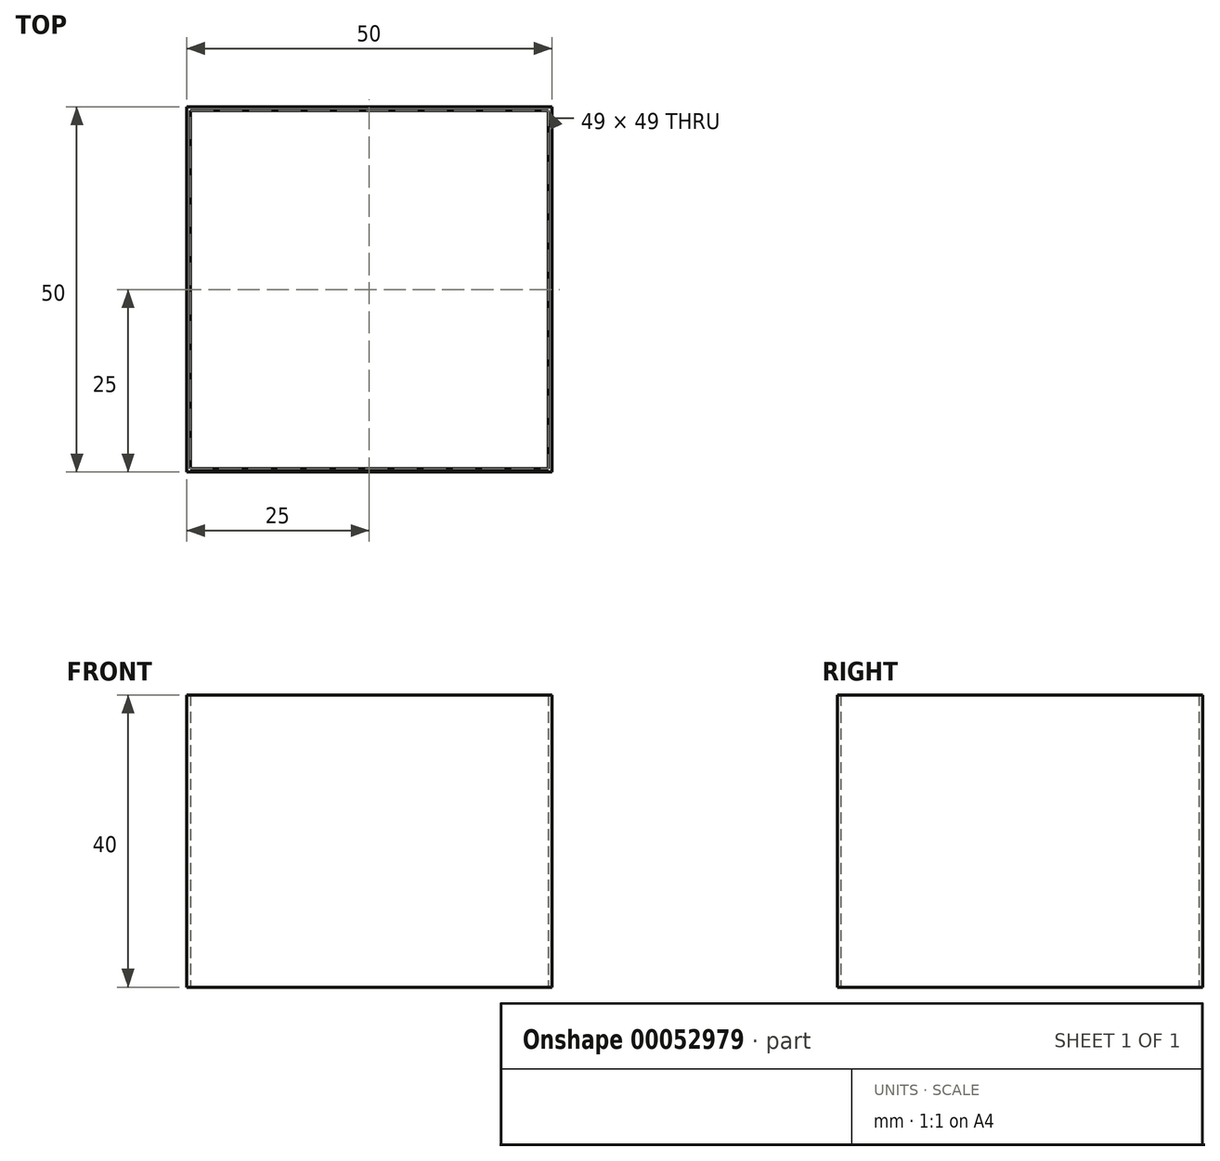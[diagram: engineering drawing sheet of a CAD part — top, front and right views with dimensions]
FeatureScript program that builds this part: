
annotation { "Feature Type Name" : "Feature", "Feature Type Description" : "" }
export const myFeature = defineFeature(function(context is Context, id is Id, definition is map)
    precondition{}
    {
        {
            var Q0;
            Q0=qCreatedBy(makeId("Top.planeOp"),FACE);
            var sketch = newSketch(context, id + "F0", { "sketchPlane" : qUnion([Q0])});
            skLineSegment(sketch, "E0.rect.bottom", {"start": v(25, -25) * mm, "end": v(-25, -25) * mm});
            skLineSegment(sketch, "E0.rect.top", {"start": v(25, 25) * mm, "end": v(-25, 25) * mm});
            skLineSegment(sketch, "E0.rect.left", {"start": v(25, -25) * mm, "end": v(25, 25) * mm});
            skLineSegment(sketch, "E0.rect.right", {"start": v(-25, -25) * mm, "end": v(-25, 25) * mm});
            skPoint(sketch, "E0.rect.middle", {"position": v(0, 0) * mm});
            skLineSegment(sketch, "E1.rect.bottom", {"start": v(24.5, -24.5) * mm, "end": v(-24.5, -24.5) * mm});
            skLineSegment(sketch, "E1.rect.top", {"start": v(24.5, 24.5) * mm, "end": v(-24.5, 24.5) * mm});
            skLineSegment(sketch, "E1.rect.left", {"start": v(24.5, -24.5) * mm, "end": v(24.5, 24.5) * mm});
            skLineSegment(sketch, "E1.rect.right", {"start": v(-24.5, -24.5) * mm, "end": v(-24.5, 24.5) * mm});
            skSolve(sketch);
        }
        {
            var Q0;
            Q0=makeQuery(id+"F0.imprint","IMPRINT",FACE,{"disambiguationData":[TD([[makeQuery(id+"F0.imprint","IMPRINT",EDGE,{"derivedFrom":sQuery(id+"F0.wireOp",EDGE,"E0.rect.bottom")}),-1.0]])]});
            extrude(context, id + "F1", {"entities" : qUnion([Q0]), "depth" : 40 * mm});
        }
    });
